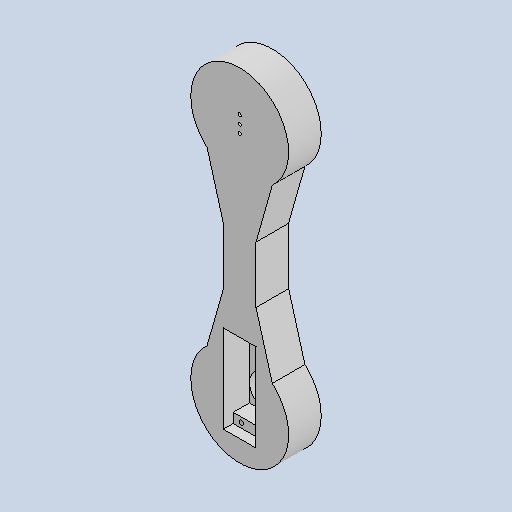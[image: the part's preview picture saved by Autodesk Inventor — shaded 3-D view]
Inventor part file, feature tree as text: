
AUTODESK INVENTOR PART (.ipt)
format: ipt  version: 2022 (Build 260153000, 153)  size: 239,104 bytes
history: native  units: in
note: dims shown in document units (in); Inventor stores cm internally (conversion verified against a paired STEP export)
features: extrude x13, sketch x13, thread x4, chamfer x1
ambient origin geometry x8: Origin, YZ Plane, XZ Plane, XY Plane, X Axis, Y Axis, Z Axis, Center Point
bodies: Solid1 (feature_tree)
feature tree (31):
  extrude  "Extrusion1"  Depth=5.9055in
  extrude  "Extrusion2"  Depth=2.3622in
  extrude  "Extrusion3"  Depth=0.7874in
  extrude  "Extrusion4"  Depth=1.4488in
  extrude  "Extrusion5"  Depth=0.2362in
  thread  "Thread1"  [1 undecoded]
  thread  "Thread2"  [1 undecoded]
  thread  "Thread3"  [1 undecoded]
  thread  "Thread4"  [1 undecoded]
  extrude  "Extrusion6"  Depth=0.2362in
  extrude  "Extrusion7"  Depth=0.2362in
  extrude  "Extrusion8"  Depth=0.1969in
  extrude  "Extrusion9"  Depth=0.1063in
  extrude  "Extrusion10"  Depth=0.1063in
  extrude  "Extrusion11"  Depth=0.3937in TaperAngle=0.0deg
  extrude  "Extrusion12"  Depth=0.3937in TaperAngle=0.0deg
  extrude  "Extrusion13"  Depth=0.3937in TaperAngle=0.0deg
  chamfer  "Chamfer2"  Distance=0.7874in
  sketch  "Sketch1"  dims[d0=1.5748in d1=5.9055in]
  sketch  "Sketch2"  dims[d2=2.3622in d3=2.3622in]
  sketch  "Sketch3"  dims[d4=0.7874in d5=0.0in d6=0.7874in]
  sketch  "Sketch4"  dims[d7=0.6693in d8=1.4488in]
  sketch  "Sketch5"  dims[d9=0.2362in d10=0.2362in d11=0.1181in d12=0.6299in d13=0.0in d14=0.7874in d15=2.7451in d16=0.0in]
  sketch  "Sketch6"  dims[d17=0.2362in d18=0.2362in]
  sketch  "Sketch7"  dims[d19=0.2362in d20=0.0in d21=0.1181in]
  sketch  "Sketch8"  dims[d22=0.1969in d23=0.1969in]
  sketch  "Sketch9"  dims[d24=0.1063in d25=0.1063in]
  sketch  "Sketch10"  dims[d26=0.1181in d27=0.1063in]
  sketch  "Sketch11"  dims[d28=0.1063in d29=0.3937in d30=0.0in]
  sketch  "Sketch12"  dims[d31=0.3937in d32=0.0in d33=0.3937in d34=0.0in]
  sketch  "Sketch13"  dims[d35=0.3937in d36=0.0in d37=0.3937in d38=0.0in d39=0.7874in d40=5.9055in d41=0.7874in d42=0.0787in d43=0.0787in d44=0.0787in d45=1.5438in d46=0.0in d47=0.7874in d48=0.6299in d49=0.0in d53=0.7874in d54=2.7559in d55=2.7559in d56=2.2313in d57=0.0in d58=0.6299in d59=0.0in d60=0.7874in d61=0.6299in d62=0.0in d63=0.7874in d64=0.0in d65=1.9626in d66=0.0in d67=0.0787in d68=0.0787in d69=1.6624in d70=0.0in d71=0.4724in d72=0.0787in d73=45.0deg]
note: 4 required parameter values undecoded (feature->parameter linkage not recoverable at this tier; creation-order binding heuristic only, values carry confidence <= 0.55)
